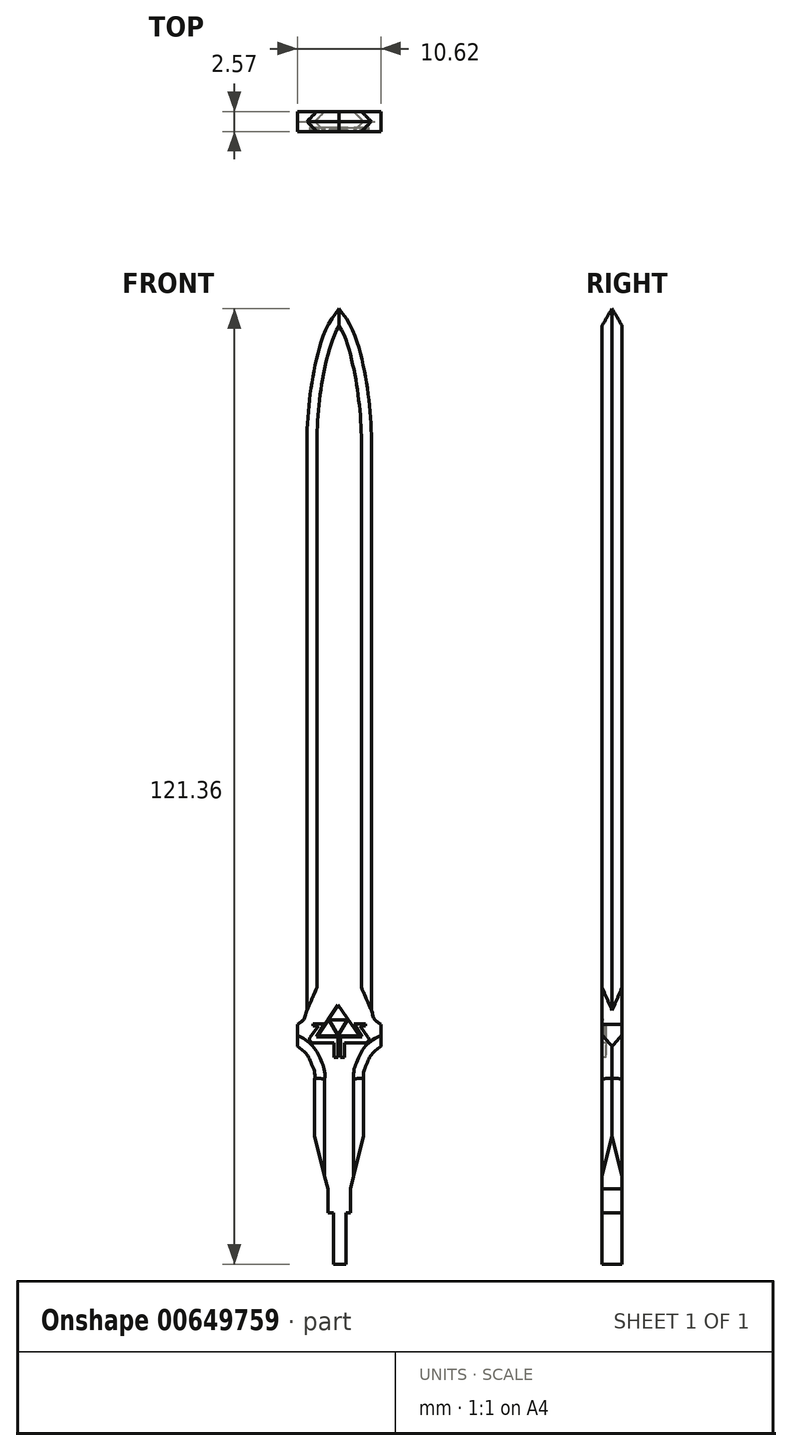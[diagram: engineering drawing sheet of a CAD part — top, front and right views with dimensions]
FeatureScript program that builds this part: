
annotation { "Feature Type Name" : "Feature", "Feature Type Description" : "" }
export const myFeature = defineFeature(function(context is Context, id is Id, definition is map)
    precondition{}
    {
        {
            var Q0;
            Q0=qCreatedBy(makeId("Front.planeOp"),FACE);
            var sketch = newSketch(context, id + "F0", { "sketchPlane" : qUnion([Q0])});
            skFitSpline(sketch, "E0", {"points": [v(0, 69.86) * mm, v(2.02, 66.4) * mm, v(4.1, 53.05) * mm], "startDerivative": vector(6.07, -7.92) * mm, "endDerivative": vector(0, -21.33) * mm});
            skLineSegment(sketch, "E1", {"start": v(4.1, 53.05) * mm, "end": v(4.1, -19.24) * mm});
            skFitSpline(sketch, "E2", {"points": [v(4.1, -19.24) * mm, v(4.46, -20.36) * mm, v(5.31, -21.07) * mm], "startDerivative": vector(1.09, -2.46) * mm, "endDerivative": vector(1.36, -1.13) * mm});
            skLineSegment(sketch, "E3", {"start": v(5.31, -21.07) * mm, "end": v(5.31, -23.85) * mm});
            skFitSpline(sketch, "E4", {"points": [v(5.31, -23.85) * mm, v(3.46, -26.2) * mm, v(3.1, -27.9) * mm], "startDerivative": vector(-7.03, -3.9) * mm, "endDerivative": vector(0.5, -6.4) * mm});
            skLineSegment(sketch, "E5", {"start": v(3.1, -27.9) * mm, "end": v(3.1, -31.4) * mm});
            skLineSegment(sketch, "E6", {"start": v(3.1, -31.4) * mm, "end": v(3.1, -32.89) * mm});
            skLineSegment(sketch, "E7", {"start": v(3.1, -32.89) * mm, "end": v(1.74, -32.6) * mm});
            skLineSegment(sketch, "E8", {"start": v(1.74, -32.6) * mm, "end": v(1.74, -33.25) * mm});
            skLineSegment(sketch, "E9", {"start": v(1.74, -33.25) * mm, "end": v(0.45, -34.84) * mm});
            skLineSegment(sketch, "E10", {"start": v(0.45, -34.84) * mm, "end": v(0, -34.47) * mm});
            skFitSpline(sketch, "E11.MirrorCS", {"points": [v(0, 69.86) * mm, v(-2.02, 66.4) * mm, v(-4.1, 53.05) * mm], "startDerivative": vector(-6.07, -7.92) * mm, "endDerivative": vector(0, -21.33) * mm});
            skLineSegment(sketch, "E12.MirrorCS", {"start": v(-4.1, 53.05) * mm, "end": v(-4.1, -19.24) * mm});
            skLineSegment(sketch, "E13.MirrorCS", {"start": v(-5.31, -21.07) * mm, "end": v(-5.31, -23.85) * mm});
            skFitSpline(sketch, "E14.MirrorCS", {"points": [v(-5.31, -23.85) * mm, v(-3.46, -26.2) * mm, v(-3.1, -27.9) * mm], "startDerivative": vector(7.03, -3.9) * mm, "endDerivative": vector(-0.5, -6.4) * mm});
            skLineSegment(sketch, "E15.MirrorCS", {"start": v(-3.1, -27.9) * mm, "end": v(-3.1, -31.4) * mm});
            skLineSegment(sketch, "E16.MirrorCS", {"start": v(-3.1, -31.4) * mm, "end": v(-3.1, -32.89) * mm});
            skLineSegment(sketch, "E17.MirrorCS", {"start": v(-3.1, -32.89) * mm, "end": v(-1.74, -32.6) * mm});
            skLineSegment(sketch, "E18.MirrorCS", {"start": v(-1.74, -32.6) * mm, "end": v(-1.74, -33.25) * mm});
            skLineSegment(sketch, "E19.MirrorCS", {"start": v(-1.74, -33.25) * mm, "end": v(-0.45, -34.84) * mm});
            skLineSegment(sketch, "E20.MirrorCS", {"start": v(-0.45, -34.84) * mm, "end": v(0, -34.47) * mm});
            skFitSpline(sketch, "E21.MirrorCS", {"points": [v(-4.1, -19.24) * mm, v(-4.46, -20.36) * mm, v(-5.31, -21.07) * mm], "startDerivative": vector(-1.09, -2.46) * mm, "endDerivative": vector(-1.36, -1.13) * mm});
            skLineSegment(sketch, "E22", {"start": v(-3.1, -32.89) * mm, "end": v(-3.1, -35.2) * mm});
            skLineSegment(sketch, "E23", {"start": v(-3.1, -35.2) * mm, "end": v(-1.44, -41.91) * mm});
            skLineSegment(sketch, "E24", {"start": v(-1.44, -41.91) * mm, "end": v(-1.44, -45) * mm});
            skLineSegment(sketch, "E25", {"start": v(-1.44, -45) * mm, "end": v(0, -45) * mm});
            skLineSegment(sketch, "E26.MirrorCS", {"start": v(3.1, -32.89) * mm, "end": v(3.1, -35.2) * mm});
            skLineSegment(sketch, "E27.MirrorCS", {"start": v(3.1, -35.2) * mm, "end": v(1.44, -41.91) * mm});
            skLineSegment(sketch, "E28.MirrorCS", {"start": v(1.44, -41.91) * mm, "end": v(1.44, -45) * mm});
            skLineSegment(sketch, "E29.MirrorCS", {"start": v(1.44, -45) * mm, "end": v(0, -45) * mm});
            skLineSegment(sketch, "E30", {"start": v(-0.72, -45) * mm, "end": v(-0.72, -51.5) * mm});
            skPoint(sketch, "E30.endSnap0", {"position": v(-0.72, -45) * mm});
            skLineSegment(sketch, "E31", {"start": v(-0.72, -51.5) * mm, "end": v(0.85, -51.5) * mm});
            skLineSegment(sketch, "E32", {"start": v(0.85, -51.5) * mm, "end": v(0.85, -45) * mm});
            skLineSegment(sketch, "E33", {"start": v(-0.14, -18.54) * mm, "end": v(-2.78, -22.54) * mm});
            skLineSegment(sketch, "E34", {"start": v(-2.78, -22.54) * mm, "end": v(2.57, -22.54) * mm});
            skLineSegment(sketch, "E35", {"start": v(2.57, -22.54) * mm, "end": v(-0.14, -18.54) * mm});
            skSolve(sketch);
        }
        {
            var Q0;
            Q0=makeQuery(id+"F0.imprint","IMPRINT",FACE,{"disambiguationData":[TD([[makeQuery(id+"F0.imprint","IMPRINT",EDGE,{"derivedFrom":sQuery(id+"F0.wireOp",EDGE,"E0")}),-1.0]])]});
            var Q1;
            Q1=makeQuery(id+"F0.imprint","IMPRINT",FACE,{"disambiguationData":[TD([[makeQuery(id+"F0.imprint","IMPRINT",EDGE,{"derivedFrom":sQuery(id+"F0.wireOp",EDGE,"E7")}),1.0]])]});
            var Q2;
            {var subQ0=sQuery(id+"F0.wireOp",EDGE,"E30");Q2=makeQuery(id+"F0.imprint","IMPRINT",FACE,{"disambiguationData":[TD([[makeQuery(id+"F0.imprint","IMPRINT",EDGE,{"derivedFrom":subQ0}),1.0]])]});}
            extrude(context, id + "F1", {"entities" : qUnion([Q0, Q1, Q2]), "depth" : 2.54 * mm, "offsetDistance" : 25.4 * mm});
        }
        {
            var Q0;
            Q0=makeQuery(id+"F1.opExtrude","CAP_EDGE",EDGE,{"disambiguationData":[OSD([sQuery(id+"F0.wireOp",EDGE,"E11.MirrorCS")])],"isStart":false});
            var Q1;
            Q1=makeQuery(id+"F1.opExtrude","CAP_EDGE",EDGE,{"disambiguationData":[OSD([sQuery(id+"F0.wireOp",EDGE,"E0")])],"isStart":false});
            var Q2;
            Q2=makeQuery(id+"F1.opExtrude","CAP_EDGE",EDGE,{"disambiguationData":[OSD([sQuery(id+"F0.wireOp",EDGE,"E1")])],"isStart":true});
            var Q3;
            Q3=makeQuery(id+"F1.opExtrude","CAP_EDGE",EDGE,{"disambiguationData":[OSD([sQuery(id+"F0.wireOp",EDGE,"E12.MirrorCS")])],"isStart":true});
            var Q4;
            Q4=makeQuery(id+"F1.opExtrude","CAP_EDGE",EDGE,{"disambiguationData":[OSD([sQuery(id+"F0.wireOp",EDGE,"E11.MirrorCS")])],"isStart":true});
            var Q5;
            Q5=makeQuery(id+"F1.opExtrude","CAP_EDGE",EDGE,{"disambiguationData":[OSD([sQuery(id+"F0.wireOp",EDGE,"E0")])],"isStart":true});
            var Q6;
            Q6=makeQuery(id+"F1.opExtrude","CAP_EDGE",EDGE,{"disambiguationData":[OSD([sQuery(id+"F0.wireOp",EDGE,"E5"),sQuery(id+"F0.wireOp",EDGE,"E6"),sQuery(id+"F0.wireOp",EDGE,"E26.MirrorCS")])],"isStart":false});
            var Q7;
            Q7=makeQuery(id+"F1.opExtrude","CAP_EDGE",EDGE,{"disambiguationData":[OSD([sQuery(id+"F0.wireOp",EDGE,"E15.MirrorCS"),sQuery(id+"F0.wireOp",EDGE,"E16.MirrorCS"),sQuery(id+"F0.wireOp",EDGE,"E22")])],"isStart":false});
            var Q8;
            Q8=makeQuery(id+"F1.opExtrude","CAP_EDGE",EDGE,{"disambiguationData":[OSD([sQuery(id+"F0.wireOp",EDGE,"E4")])],"isStart":false});
            var Q9;
            Q9=makeQuery(id+"F1.opExtrude","CAP_EDGE",EDGE,{"disambiguationData":[OSD([sQuery(id+"F0.wireOp",EDGE,"E14.MirrorCS")])],"isStart":false});
            var Q10;
            Q10=makeQuery(id+"F1.opExtrude","CAP_EDGE",EDGE,{"disambiguationData":[OSD([sQuery(id+"F0.wireOp",EDGE,"E4")])],"isStart":true});
            var Q11;
            Q11=makeQuery(id+"F1.opExtrude","CAP_EDGE",EDGE,{"disambiguationData":[OSD([sQuery(id+"F0.wireOp",EDGE,"E5"),sQuery(id+"F0.wireOp",EDGE,"E6"),sQuery(id+"F0.wireOp",EDGE,"E26.MirrorCS")])],"isStart":true});
            var Q12;
            Q12=makeQuery(id+"F1.opExtrude","CAP_EDGE",EDGE,{"disambiguationData":[OSD([sQuery(id+"F0.wireOp",EDGE,"E15.MirrorCS"),sQuery(id+"F0.wireOp",EDGE,"E16.MirrorCS"),sQuery(id+"F0.wireOp",EDGE,"E22")])],"isStart":true});
            var Q13;
            Q13=makeQuery(id+"F1.opExtrude","CAP_EDGE",EDGE,{"disambiguationData":[OSD([sQuery(id+"F0.wireOp",EDGE,"E14.MirrorCS")])],"isStart":true});
            chamfer(context, id + "F2", {"entities" : qUnion([Q0, Q1, Q2, Q3, Q4, Q5, Q6, Q7, Q8, Q9, Q10, Q11, Q12, Q13]), "width" : 1.27 * mm, "tangentPropagation" : true});
        }
        {
            var Q0;
            Q0=makeQuery(id+"F0.imprint","IMPRINT",FACE,{"disambiguationData":[TD([[makeQuery(id+"F0.imprint","IMPRINT",EDGE,{"derivedFrom":sQuery(id+"F0.wireOp",EDGE,"E33")}),1.0]])]});
            extrude(context, id + "F3", {"entities" : qUnion([Q0]), "operationType" : NewBodyOperationType.ADD, "depth" : 2.57 * mm, "offsetDistance" : 25.4 * mm});
        }
        {
            var Q0;
            Q0=makeQuery(id+"F3.opExtrude","CAP_FACE",FACE,{"disambiguationData":[OSD([sQuery(id+"F0.wireOp",EDGE,"E33"),sQuery(id+"F0.wireOp",EDGE,"E34"),sQuery(id+"F0.wireOp",EDGE,"E35")])],"isStart":false});
            var sketch = newSketch(context, id + "F4", { "sketchPlane" : qUnion([Q0])});
            skLineSegment(sketch, "E36", {"start": v(-1.3, -20.48) * mm, "end": v(1.09, -20.48) * mm});
            skLineSegment(sketch, "E37", {"start": v(1.09, -20.48) * mm, "end": v(-0.14, -22.45) * mm});
            skLineSegment(sketch, "E38", {"start": v(-0.14, -22.45) * mm, "end": v(-1.3, -20.48) * mm});
            skSolve(sketch);
        }
        {
            var Q0;
            Q0=makeQuery(id+"F4.imprint","IMPRINT",FACE,{"disambiguationData":[TD([[makeQuery(id+"F4.imprint","IMPRINT",EDGE,{"derivedFrom":sQuery(id+"F4.wireOp",EDGE,"E36")}),-1.0]])]});
            extrude(context, id + "F5", {"entities" : qUnion([Q0]), "operationType" : NewBodyOperationType.REMOVE, "oppositeDirection" : true, "depth" : 0.25 * mm, "offsetDistance" : 25.4 * mm});
        }
        {
            var Q0;
            Q0=makeQuery(id+"F1.opExtrude","CAP_FACE",FACE,{"disambiguationData":[OSD([sQuery(id+"F0.wireOp",EDGE,"E0"),sQuery(id+"F0.wireOp",EDGE,"E1"),sQuery(id+"F0.wireOp",EDGE,"E2"),sQuery(id+"F0.wireOp",EDGE,"E3"),sQuery(id+"F0.wireOp",EDGE,"E4"),sQuery(id+"F0.wireOp",EDGE,"E5"),sQuery(id+"F0.wireOp",EDGE,"E6"),sQuery(id+"F0.wireOp",EDGE,"E11.MirrorCS"),sQuery(id+"F0.wireOp",EDGE,"E12.MirrorCS"),sQuery(id+"F0.wireOp",EDGE,"E13.MirrorCS"),sQuery(id+"F0.wireOp",EDGE,"E14.MirrorCS"),sQuery(id+"F0.wireOp",EDGE,"E15.MirrorCS"),sQuery(id+"F0.wireOp",EDGE,"E16.MirrorCS"),sQuery(id+"F0.wireOp",EDGE,"E21.MirrorCS"),sQuery(id+"F0.wireOp",EDGE,"E22"),sQuery(id+"F0.wireOp",EDGE,"E23"),sQuery(id+"F0.wireOp",EDGE,"E24"),sQuery(id+"F0.wireOp",EDGE,"E25"),sQuery(id+"F0.wireOp",EDGE,"E26.MirrorCS"),sQuery(id+"F0.wireOp",EDGE,"E27.MirrorCS"),sQuery(id+"F0.wireOp",EDGE,"E28.MirrorCS"),sQuery(id+"F0.wireOp",EDGE,"E29.MirrorCS"),sQuery(id+"F0.wireOp",EDGE,"E30"),sQuery(id+"F0.wireOp",EDGE,"E31"),sQuery(id+"F0.wireOp",EDGE,"E32"),sQuery(id+"F0.wireOp",EDGE,"E33"),sQuery(id+"F0.wireOp",EDGE,"E34"),sQuery(id+"F0.wireOp",EDGE,"E35")])],"isStart":false});
            var sketch = newSketch(context, id + "F6", { "sketchPlane" : qUnion([Q0])});
            skLineSegment(sketch, "E39", {"start": v(3.34, -20.95) * mm, "end": v(3.34, -21.2) * mm});
            skLineSegment(sketch, "E40", {"start": v(3.34, -21.2) * mm, "end": v(2.64, -21.2) * mm});
            skLineSegment(sketch, "E41", {"start": v(2.64, -21.2) * mm, "end": v(3.7, -22.69) * mm});
            skFitSpline(sketch, "E42", {"points": [v(3.7, -22.69) * mm, v(3.77, -23.01) * mm, v(3.45, -23.4) * mm], "startDerivative": vector(0.56, -0.73) * mm, "endDerivative": vector(-0.7, -0.6) * mm});
            skLineSegment(sketch, "E43", {"start": v(3.45, -23.4) * mm, "end": v(0.68, -23.4) * mm});
            skLineSegment(sketch, "E44", {"start": v(0.68, -23.4) * mm, "end": v(0.68, -25.23) * mm});
            skLineSegment(sketch, "E45", {"start": v(0.68, -25.23) * mm, "end": v(0.14, -25.23) * mm});
            skLineSegment(sketch, "E46", {"start": v(0.14, -25.23) * mm, "end": v(0.14, -22.97) * mm});
            skFitSpline(sketch, "E47", {"points": [v(0.14, -22.97) * mm, v(0.2, -22.76) * mm, v(0.52, -22.62) * mm], "startDerivative": vector(0, 0.48) * mm, "endDerivative": vector(0.98, 0.17) * mm});
            skLineSegment(sketch, "E48", {"start": v(0.52, -22.62) * mm, "end": v(2.88, -22.62) * mm});
            skLineSegment(sketch, "E49", {"start": v(2.88, -22.62) * mm, "end": v(1.87, -20.95) * mm});
            skLineSegment(sketch, "E50", {"start": v(1.87, -20.95) * mm, "end": v(3.34, -20.95) * mm});
            skLineSegment(sketch, "E51.MirrorCS", {"start": v(-0.14, -25.23) * mm, "end": v(-0.14, -22.97) * mm});
            skLineSegment(sketch, "E52.MirrorCS", {"start": v(-0.68, -23.4) * mm, "end": v(-0.68, -25.23) * mm});
            skLineSegment(sketch, "E53.MirrorCS", {"start": v(-0.68, -25.23) * mm, "end": v(-0.14, -25.23) * mm});
            skFitSpline(sketch, "E54.MirrorCS", {"points": [v(-0.14, -22.97) * mm, v(-0.2, -22.76) * mm, v(-0.52, -22.62) * mm], "startDerivative": vector(0, 0.48) * mm, "endDerivative": vector(-0.98, 0.17) * mm});
            skLineSegment(sketch, "E55.MirrorCS", {"start": v(-0.52, -22.62) * mm, "end": v(-2.88, -22.62) * mm});
            skLineSegment(sketch, "E56.MirrorCS", {"start": v(-3.45, -23.4) * mm, "end": v(-0.68, -23.4) * mm});
            skFitSpline(sketch, "E57.MirrorCS", {"points": [v(-3.7, -22.69) * mm, v(-3.77, -23.01) * mm, v(-3.45, -23.4) * mm], "startDerivative": vector(-0.56, -0.73) * mm, "endDerivative": vector(0.7, -0.6) * mm});
            skLineSegment(sketch, "E58.MirrorCS", {"start": v(-2.64, -21.2) * mm, "end": v(-3.7, -22.69) * mm});
            skLineSegment(sketch, "E59.MirrorCS", {"start": v(-2.88, -22.62) * mm, "end": v(-1.87, -20.95) * mm});
            skLineSegment(sketch, "E60.MirrorCS", {"start": v(-3.34, -21.2) * mm, "end": v(-2.64, -21.2) * mm});
            skLineSegment(sketch, "E61.MirrorCS", {"start": v(-3.34, -20.95) * mm, "end": v(-3.34, -21.2) * mm});
            skLineSegment(sketch, "E62.MirrorCS", {"start": v(-1.87, -20.95) * mm, "end": v(-3.34, -20.95) * mm});
            skSolve(sketch);
        }
        {
            var Q0;
            Q0=makeQuery(id+"F6.imprint","IMPRINT",FACE,{"disambiguationData":[TD([[makeQuery(id+"F6.imprint","IMPRINT",EDGE,{"derivedFrom":sQuery(id+"F6.wireOp",EDGE,"E51.MirrorCS")}),1.0]])]});
            var Q1;
            Q1=makeQuery(id+"F6.imprint","IMPRINT",FACE,{"disambiguationData":[TD([[makeQuery(id+"F6.imprint","IMPRINT",EDGE,{"derivedFrom":sQuery(id+"F6.wireOp",EDGE,"E39")}),-1.0]])]});
            extrude(context, id + "F7", {"entities" : qUnion([Q0, Q1]), "operationType" : NewBodyOperationType.REMOVE, "oppositeDirection" : true, "depth" : 0.5 * mm, "offsetDistance" : 25.4 * mm});
        }
    });
